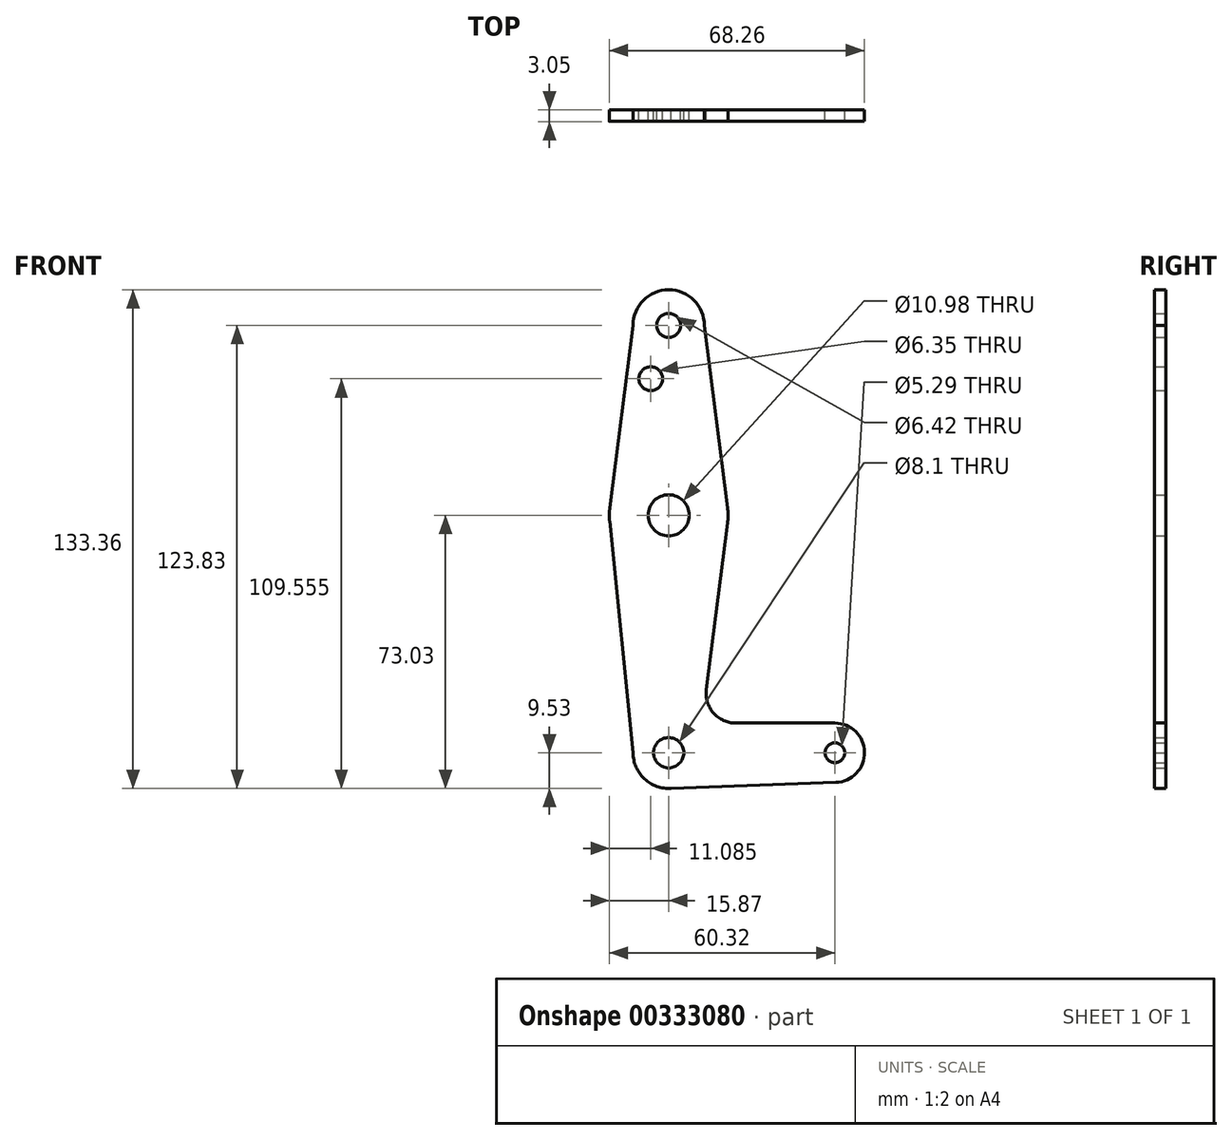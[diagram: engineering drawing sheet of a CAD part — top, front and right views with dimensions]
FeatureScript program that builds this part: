
annotation { "Feature Type Name" : "Feature", "Feature Type Description" : "" }
export const myFeature = defineFeature(function(context is Context, id is Id, definition is map)
    precondition{}
    {
        {
            var Q0;
            Q0=qCreatedBy(makeId("Front.planeOp"),FACE);
            var sketch = newSketch(context, id + "F0", { "sketchPlane" : qUnion([Q0])});
            skLineSegment(sketch, "E0", {"start": v(0, 0) * mm, "end": v(0, 114.3) * mm, "construction": true});
            skLineSegment(sketch, "E1", {"start": v(0, 0) * mm, "end": v(44.45, 0) * mm, "construction": true});
            skCircle(sketch, "E2", {"center": v(0, 114.3) * mm, "radius": 9.53 * mm});
            skCircle(sketch, "E3", {"center": v(0, 63.5) * mm, "radius": 15.88 * mm});
            skCircle(sketch, "E4", {"center": v(0, 0) * mm, "radius": 9.53 * mm});
            skCircle(sketch, "E5", {"center": v(44.45, 0) * mm, "radius": 7.94 * mm});
            skLineSegment(sketch, "E6", {"start": v(-9.52, 114.3) * mm, "end": v(-15.75, 65.5) * mm});
            skLineSegment(sketch, "E7", {"start": v(9.53, 114.3) * mm, "end": v(15.75, 65.5) * mm});
            skLineSegment(sketch, "E8", {"start": v(0, -9.53) * mm, "end": v(44.73, -7.93) * mm});
            skLineSegment(sketch, "E9", {"start": v(-9.53, 0) * mm, "end": v(-15.8, 61.9) * mm});
            skLineSegment(sketch, "E10", {"start": v(15.75, 61.5) * mm, "end": v(10.06, 16.9) * mm});
            skLineSegment(sketch, "E11", {"start": v(17.95, 7.94) * mm, "end": v(44.45, 7.94) * mm});
            skArc(sketch, "E12.filletArc", {"start": v(10.06, 16.9) * mm, "mid": v(11.98, 10.63) * mm, "end": v(17.95, 7.94) * mm});
            skCircle(sketch, "E13", {"center": v(44.45, 0) * mm, "radius": 2.65 * mm});
            skCircle(sketch, "E14", {"center": v(0, 0) * mm, "radius": 4.05 * mm});
            skCircle(sketch, "E15", {"center": v(0, 63.5) * mm, "radius": 5.5 * mm});
            skCircle(sketch, "E16", {"center": v(0, 114.3) * mm, "radius": 3.21 * mm});
            skCircle(sketch, "E17", {"center": v(-4.78, 100.03) * mm, "radius": 3.18 * mm});
            skSolve(sketch);
        }
        {
            var Q0;
            Q0 = qSketchRegion(id + "F0", true);
            extrude(context, id + "F1", {"entities" : qUnion([Q0]), "depth" : 3.05 * mm});
        }
    });
